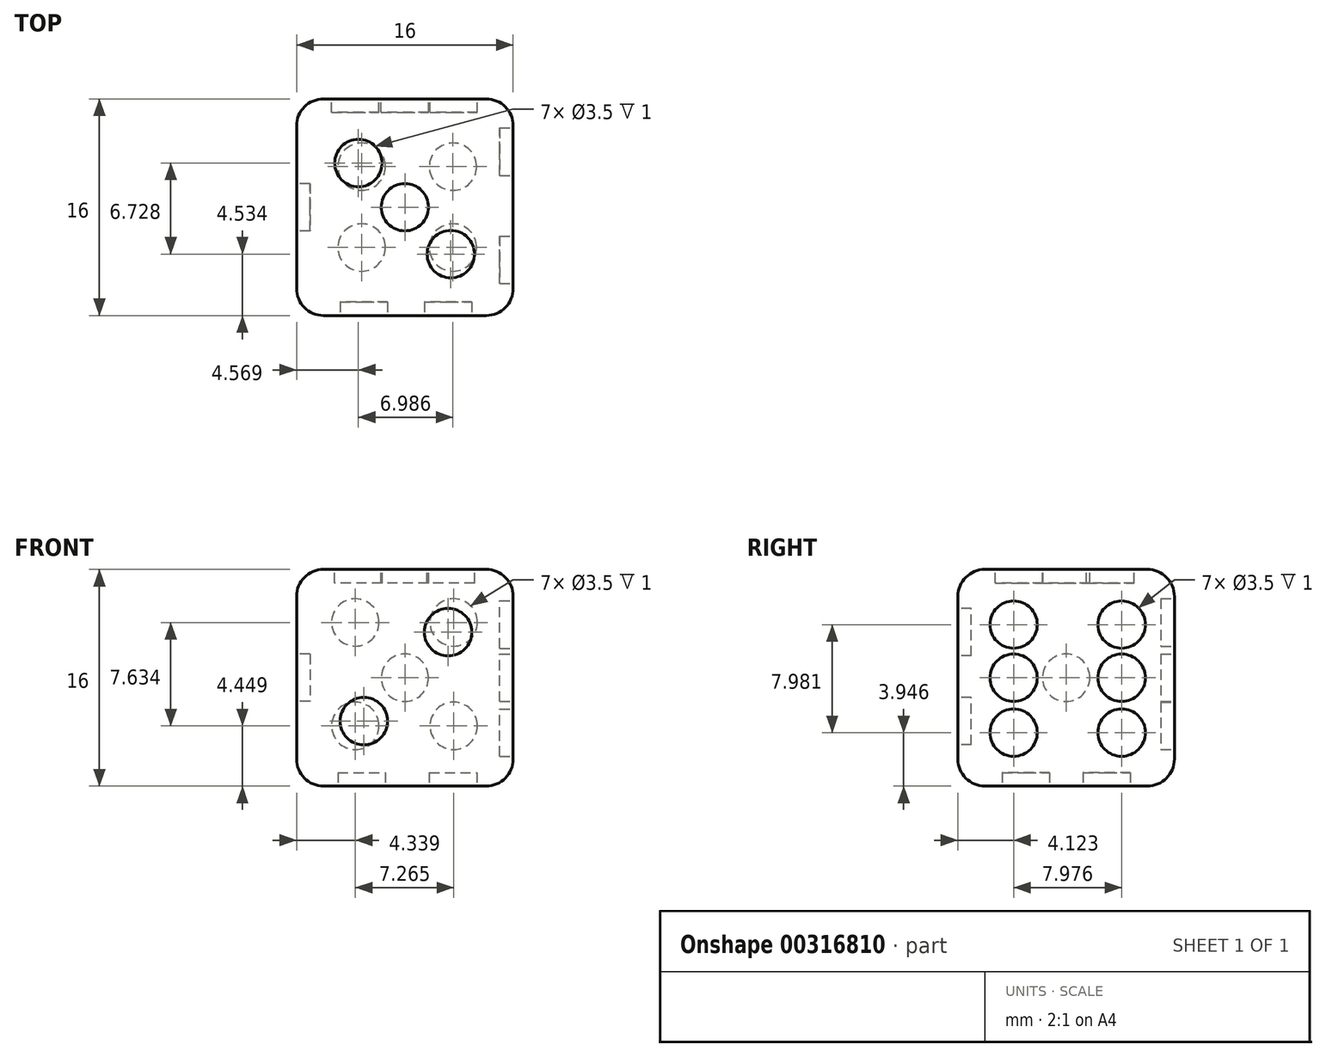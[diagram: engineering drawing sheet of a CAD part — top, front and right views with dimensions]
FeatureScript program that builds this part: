
annotation { "Feature Type Name" : "Feature", "Feature Type Description" : "" }
export const myFeature = defineFeature(function(context is Context, id is Id, definition is map)
    precondition{}
    {
        {
            var Q0;
            Q0=qCreatedBy(makeId("Front.planeOp"),FACE);
            var sketch = newSketch(context, id + "F0", { "sketchPlane" : qUnion([Q0])});
            skLineSegment(sketch, "E0.bottom", {"start": v(-8, 8) * mm, "end": v(8, 8) * mm});
            skLineSegment(sketch, "E0.top", {"start": v(-8, -8) * mm, "end": v(8, -8) * mm});
            skLineSegment(sketch, "E0.left", {"start": v(-8, 8) * mm, "end": v(-8, -8) * mm});
            skLineSegment(sketch, "E0.right", {"start": v(8, 8) * mm, "end": v(8, -8) * mm});
            skPoint(sketch, "E0.middle", {"position": v(0, 0) * mm});
            skSolve(sketch);
        }
        {
            var Q0;
            Q0 = qSketchRegion(id + "F0", true);
            extrude(context, id + "F1", {"entities" : qUnion([Q0]), "endBound" : BoundingType.SYMMETRIC, "depth" : 16 * mm});
        }
        {
            var Q0;
            Q0=makeQuery(id+"F1.opExtrude","CAP_EDGE",EDGE,{"disambiguationData":[OSD([sQuery(id+"F0.wireOp",EDGE,"E0.bottom")])],"isStart":false});
            var Q1;
            Q1=makeQuery(id+"F1.opExtrude","SWEPT_EDGE",EDGE,{"disambiguationData":[OSD([sQuery(id+"F0.wireOp",EDGE,"E0.bottom"),sQuery(id+"F0.wireOp",EDGE,"E0.right")])]});
            var Q2;
            Q2=makeQuery(id+"F1.opExtrude","CAP_EDGE",EDGE,{"disambiguationData":[OSD([sQuery(id+"F0.wireOp",EDGE,"E0.right")])],"isStart":false});
            var Q3;
            Q3=makeQuery(id+"F1.opExtrude","CAP_EDGE",EDGE,{"disambiguationData":[OSD([sQuery(id+"F0.wireOp",EDGE,"E0.right")])],"isStart":true});
            var Q4;
            Q4=makeQuery(id+"F1.opExtrude","SWEPT_EDGE",EDGE,{"disambiguationData":[OSD([sQuery(id+"F0.wireOp",EDGE,"E0.top"),sQuery(id+"F0.wireOp",EDGE,"E0.right")])]});
            var Q5;
            Q5=makeQuery(id+"F1.opExtrude","CAP_EDGE",EDGE,{"disambiguationData":[OSD([sQuery(id+"F0.wireOp",EDGE,"E0.top")])],"isStart":false});
            var Q6;
            Q6=makeQuery(id+"F1.opExtrude","CAP_EDGE",EDGE,{"disambiguationData":[OSD([sQuery(id+"F0.wireOp",EDGE,"E0.top")])],"isStart":true});
            var Q7;
            Q7=makeQuery(id+"F1.opExtrude","CAP_EDGE",EDGE,{"disambiguationData":[OSD([sQuery(id+"F0.wireOp",EDGE,"E0.bottom")])],"isStart":true});
            var Q8;
            Q8=makeQuery(id+"F1.opExtrude","CAP_EDGE",EDGE,{"disambiguationData":[OSD([sQuery(id+"F0.wireOp",EDGE,"E0.left")])],"isStart":true});
            var Q9;
            Q9=makeQuery(id+"F1.opExtrude","CAP_EDGE",EDGE,{"disambiguationData":[OSD([sQuery(id+"F0.wireOp",EDGE,"E0.left")])],"isStart":false});
            var Q10;
            Q10=makeQuery(id+"F1.opExtrude","SWEPT_EDGE",EDGE,{"disambiguationData":[OSD([sQuery(id+"F0.wireOp",EDGE,"E0.top"),sQuery(id+"F0.wireOp",EDGE,"E0.left")])]});
            var Q11;
            Q11=makeQuery(id+"F1.opExtrude","SWEPT_EDGE",EDGE,{"disambiguationData":[OSD([sQuery(id+"F0.wireOp",EDGE,"E0.bottom"),sQuery(id+"F0.wireOp",EDGE,"E0.left")])]});
            fillet(context, id + "F2", {"entities" : qUnion([Q0, Q1, Q2, Q3, Q4, Q5, Q6, Q7, Q8, Q9, Q10, Q11]), "radius" : 2 * mm, "tangentPropagation" : true, "allowEdgeOverflow" : false});
        }
        {
            var Q0;
            Q0=makeQuery(id+"F1.opExtrude","SWEPT_FACE",FACE,{"disambiguationData":[OSD([sQuery(id+"F0.wireOp",EDGE,"E0.left")])]});
            var sketch = newSketch(context, id + "F3", { "sketchPlane" : qUnion([Q0])});
            skCircle(sketch, "E1", {"center": v(0, 0) * mm, "radius": 1.75 * mm});
            skSolve(sketch);
        }
        {
            var Q0;
            Q0 = qSketchRegion(id + "F3", true);
            extrude(context, id + "F4", {"entities" : qUnion([Q0]), "operationType" : NewBodyOperationType.REMOVE, "oppositeDirection" : true, "depth" : 1 * mm});
        }
        {
            var Q0;
            Q0=makeQuery(id+"F1.opExtrude","CAP_FACE",FACE,{"disambiguationData":[OSD([sQuery(id+"F0.wireOp",EDGE,"E0.bottom"),sQuery(id+"F0.wireOp",EDGE,"E0.top"),sQuery(id+"F0.wireOp",EDGE,"E0.left"),sQuery(id+"F0.wireOp",EDGE,"E0.right")])],"isStart":false});
            var sketch = newSketch(context, id + "F5", { "sketchPlane" : qUnion([Q0])});
            skCircle(sketch, "E2", {"center": v(3.2, 3.37) * mm, "radius": 1.75 * mm});
            skCircle(sketch, "E3", {"center": v(-3.03, -3.2) * mm, "radius": 1.75 * mm});
            skSolve(sketch);
        }
        {
            var Q0;
            Q0 = qSketchRegion(id + "F5", true);
            extrude(context, id + "F6", {"entities" : qUnion([Q0]), "operationType" : NewBodyOperationType.REMOVE, "oppositeDirection" : true, "depth" : 1 * mm});
        }
        {
            var Q0;
            Q0=makeQuery(id+"F1.opExtrude","SWEPT_FACE",FACE,{"disambiguationData":[OSD([sQuery(id+"F0.wireOp",EDGE,"E0.right")])]});
            var sketch = newSketch(context, id + "F7", { "sketchPlane" : qUnion([Q0])});
            skCircle(sketch, "E4", {"center": v(-3.88, 3.93) * mm, "radius": 1.75 * mm});
            skCircle(sketch, "E5", {"center": v(-3.88, 0) * mm, "radius": 1.75 * mm});
            skCircle(sketch, "E6", {"center": v(-3.88, -4.05) * mm, "radius": 1.75 * mm});
            skCircle(sketch, "E7", {"center": v(4.1, 3.93) * mm, "radius": 1.75 * mm});
            skCircle(sketch, "E8", {"center": v(4.1, 0) * mm, "radius": 1.75 * mm});
            skCircle(sketch, "E9", {"center": v(4.1, -4.05) * mm, "radius": 1.75 * mm});
            skSolve(sketch);
        }
        {
            var Q0;
            Q0 = qSketchRegion(id + "F7", true);
            extrude(context, id + "F8", {"entities" : qUnion([Q0]), "operationType" : NewBodyOperationType.REMOVE, "oppositeDirection" : true, "depth" : 1 * mm});
        }
        {
            var Q0;
            Q0=makeQuery(id+"F1.opExtrude","CAP_FACE",FACE,{"disambiguationData":[OSD([sQuery(id+"F0.wireOp",EDGE,"E0.bottom"),sQuery(id+"F0.wireOp",EDGE,"E0.top"),sQuery(id+"F0.wireOp",EDGE,"E0.left"),sQuery(id+"F0.wireOp",EDGE,"E0.right")])],"isStart":true});
            var sketch = newSketch(context, id + "F9", { "sketchPlane" : qUnion([Q0])});
            skCircle(sketch, "E10", {"center": v(0, 0) * mm, "radius": 1.75 * mm});
            skCircle(sketch, "E11", {"center": v(3.66, 4.08) * mm, "radius": 1.75 * mm});
            skCircle(sketch, "E12", {"center": v(-3.6, 4.08) * mm, "radius": 1.75 * mm});
            skCircle(sketch, "E13", {"center": v(-3.6, -3.55) * mm, "radius": 1.75 * mm});
            skCircle(sketch, "E14", {"center": v(3.66, -3.55) * mm, "radius": 1.75 * mm});
            skSolve(sketch);
        }
        {
            var Q0;
            Q0 = qSketchRegion(id + "F9", true);
            extrude(context, id + "F10", {"entities" : qUnion([Q0]), "operationType" : NewBodyOperationType.REMOVE, "oppositeDirection" : true, "depth" : 1 * mm});
        }
        {
            var Q0;
            Q0=makeQuery(id+"F1.opExtrude","SWEPT_FACE",FACE,{"disambiguationData":[OSD([sQuery(id+"F0.wireOp",EDGE,"E0.bottom")])]});
            var sketch = newSketch(context, id + "F11", { "sketchPlane" : qUnion([Q0])});
            skCircle(sketch, "E15", {"center": v(0, 0) * mm, "radius": 1.75 * mm});
            skCircle(sketch, "E16", {"center": v(3.4, -3.47) * mm, "radius": 1.75 * mm});
            skCircle(sketch, "E17", {"center": v(-3.43, 3.26) * mm, "radius": 1.75 * mm});
            skSolve(sketch);
        }
        {
            var Q0;
            Q0 = qSketchRegion(id + "F11", true);
            extrude(context, id + "F12", {"entities" : qUnion([Q0]), "operationType" : NewBodyOperationType.REMOVE, "oppositeDirection" : true, "depth" : 1 * mm});
        }
        {
            var Q0;
            Q0=makeQuery(id+"F1.opExtrude","SWEPT_FACE",FACE,{"disambiguationData":[OSD([sQuery(id+"F0.wireOp",EDGE,"E0.top")])]});
            var sketch = newSketch(context, id + "F13", { "sketchPlane" : qUnion([Q0])});
            skCircle(sketch, "E18", {"center": v(-3.2, 2.97) * mm, "radius": 1.75 * mm});
            skCircle(sketch, "E19", {"center": v(3.55, 2.97) * mm, "radius": 1.75 * mm});
            skCircle(sketch, "E20", {"center": v(3.55, -3) * mm, "radius": 1.75 * mm});
            skCircle(sketch, "E21", {"center": v(-3.2, -3) * mm, "radius": 1.75 * mm});
            skSolve(sketch);
        }
        {
            var Q0;
            Q0 = qSketchRegion(id + "F13", true);
            extrude(context, id + "F14", {"entities" : qUnion([Q0]), "operationType" : NewBodyOperationType.REMOVE, "oppositeDirection" : true, "depth" : 1 * mm});
        }
    });
